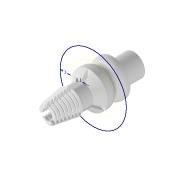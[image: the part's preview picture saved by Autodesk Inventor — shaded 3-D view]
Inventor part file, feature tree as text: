
AUTODESK INVENTOR PART (.ipt)
format: ipt  version: 2022 (Build 260153000, 153)  size: 1,178,624 bytes
history: native  units: in
note: dims shown in document units (in); Inventor stores cm internally (conversion verified against a paired STEP export)
features: sketch x15, extrude x8, other x6, revolve x4, reference x4, projected_geometry x2, plane x1, sweep x1, chamfer x1, fillet x1
ambient origin geometry x8: Origin, YZ Plane, XZ Plane, XY Plane, X Axis, Y Axis, Z Axis, Center Point
bodies: Solid1 (feature_tree)
feature tree (43):
  other  "00_selfcenter_2mm_thread_v1.ipt"
  revolve  "Revolution1"  [1 undecoded]
  extrude  "Extrusion2"  TaperAngle=0.0deg  [1 undecoded]
  sketch  "Sketch4"  dims[d11=0.3937in d12=360.0deg]
  plane  "Work Plane1"
  revolve  "Revolution2"  Angle=360.0deg
  sweep  "Sweep1"
  revolve  "Revolution3"  [1 undecoded]
  extrude  "Extrusion4"  TaperAngle=0.0deg  [1 undecoded]
  extrude  "Extrusion5"  Depth=0.3937in
  extrude  "Extrusion6"  TaperAngle=0.0deg  [1 undecoded]
  chamfer  "Chamfer1"  Distance=0.3937in
  extrude  "Extrusion8"  Depth=0.2362in
  extrude  "Extrusion9"  Depth=0.2362in
  extrude  "Extrusion10"  Depth=0.2362in
  revolve  "Revolution4"  [1 undecoded]
  fillet  "Fillet2"  Radius=0.0394in
  extrude  "Extrusion11"  Depth=0.2362in TaperAngle=45.0deg
  sketch  "Sketch2"  dims[d4=0.2165in d5=0.0984in]
  sketch  "Sketch3"  dims[d7=0.0394in d10=0.0in]
  projected_geometry  "Projected Loop1"
  reference  "Reference3"
  reference  "Reference4"
  sketch  "Sketch5"  dims[d14=0.0787in d15=0.0591in]
  sketch  "3D Sketch1"
  other  "Helical Curve1"
  sketch  "Sketch7"  dims[d16=0.0in d17=0.0in d18=0.0039in]
  sketch  "Sketch8"  dims[d19=0.1181in d22=0.0in]
  sketch  "Sketch9"  dims[d23=0.3937in d24=0.0394in]
  reference  "Reference6"
  projected_geometry  "Projected Loop2"
  sketch  "Sketch10"  dims[d25=360.0deg]
  sketch  "Sketch11"  dims[d26=0.0in d27=0.0in d28=0.0394in d29=0.0977in d30=0.29in d31=3.1496in d32=0.1872in d39=0.0in d40=0.0in]
  sketch  "Sketch13"  dims[d41=0.0394in]
  sketch  "Sketch14"  dims[d42=90.0deg]
  sketch  "Sketch15"  dims[d43=0.0591in]
  reference  "Reference7"
  sketch  "Sketch16"  dims[d44=0.0394in d45=0.3937in d46=0.0in]
  sketch  "Sketch17"  dims[d47=1.1811in d49=360.0deg d51=0.2362in d52=0.29in d53=0.1969in d54=0.1575in d55=0.0in d56=0.0394in d57=0.0in d58=0.0787in d59=0.0787in d60=45.0deg d67=0.0in d68=0.0in d69=0.0in d70=0.0in d71=0.2362in d72=0.0in d73=0.0787in d74=90.0deg d75=0.0787in d76=0.1181in d77=0.0in d78=0.0in]
  other  "Assembly_Cube_Lightsheet_FEPTube_Rotational_v3.iam"
  other  "00_Bearing_US:1"
  other  "<userpath>\Documents\Inventor\Guinardia\INVENTOR\Assembly_Guinardia_V0.iam"
  other  "Assembly_Guinardia_V0.iam"
note: 6 required parameter values undecoded (feature->parameter linkage not recoverable at this tier; creation-order binding heuristic only, values carry confidence <= 0.55)